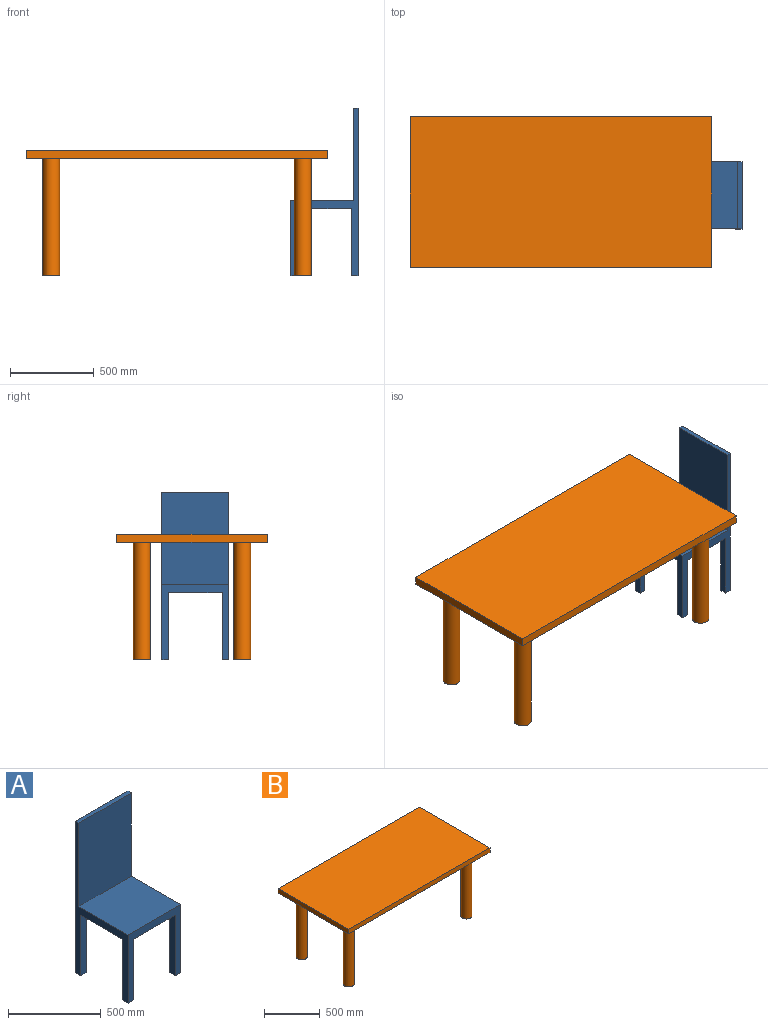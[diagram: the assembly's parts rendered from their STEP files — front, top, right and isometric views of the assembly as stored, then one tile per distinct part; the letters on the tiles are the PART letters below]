
ASSEMBLY  parts=2 mates=1
PART A: 20 faces, bbox 400x400x1000 mm
  f0: plane 1000x400mm, normal (1,0,0), area 65750mm2, adj f1,f3,f4,f5,f6,f7,f15,f16
  f1: plane 1000x400mm, normal (0,1,0), area 272000mm2, adj f0,f2,f4,f7,f11,f13,f18,f19
  f2: plane 1000x400mm, normal (-1,0,0), area 65750mm2, adj f1,f3,f4,f5,f6,f7,f8,f10
  f3: plane 450x400mm, normal (0,-1,0), area 52000mm2, adj f0,f2,f4,f5,f9,f10,f14,f16
  f4: plane 400x400mm, normal (0,0,-1), area 153600mm2, adj f0,f1,f2,f3,f8,f9,f11,f12
  f5: plane 400x375mm, normal (0,0,1), area 150000mm2, adj f0,f2,f3,f6
  f6: plane 550x400mm, normal (0,-1,0), area 220000mm2, adj f0,f2,f5,f7
  f7: plane 400x25mm, normal (0,0,1), area 10000mm2, adj f0,f1,f2,f6
  f8: plane 400x40mm, normal (0,1,0), area 16000mm2, adj f2,f4,f9,f10
  f9: plane 400x40mm, normal (1,0,0), area 16000mm2, adj f3,f4,f8,f10
  f10: plane 40x40mm, normal (0,0,-1), area 1600mm2, adj f2,f3,f8,f9
  f11: plane 400x40mm, normal (1,0,0), area 16000mm2, adj f1,f4,f12,f13
  f12: plane 400x40mm, normal (0,-1,0), area 16000mm2, adj f2,f4,f11,f13
  f13: plane 40x40mm, normal (0,0,-1), area 1600mm2, adj f1,f2,f11,f12
  f14: plane 400x40mm, normal (-1,0,0), area 16000mm2, adj f3,f4,f15,f16
  f15: plane 400x40mm, normal (0,1,0), area 16000mm2, adj f0,f4,f14,f16
  f16: plane 40x40mm, normal (0,0,-1), area 1600mm2, adj f0,f3,f14,f15
  f17: plane 400x40mm, normal (0,-1,0), area 16000mm2, adj f0,f4,f18,f19
  f18: plane 400x40mm, normal (-1,0,0), area 16000mm2, adj f1,f4,f17,f19
  f19: plane 40x40mm, normal (0,0,-1), area 1600mm2, adj f0,f1,f17,f18
PART B: 14 faces, bbox 1800x900x750 mm
  f0: plane 900x50mm, normal (1,0,0), area 45000mm2, adj f1,f3,f4,f5
  f1: plane 1800x50mm, normal (0,1,0), area 90000mm2, adj f0,f2,f4,f5
  f2: plane 900x50mm, normal (-1,0,0), area 45000mm2, adj f1,f3,f4,f5
  f3: plane 1800x50mm, normal (0,-1,0), area 90000mm2, adj f0,f2,f4,f5
  f4: plane 1800x900mm, normal (0,0,1), area 1620000mm2, adj f0,f1,f2,f3
  f5: plane 1800x900mm, normal (0,0,-1), area 1588584.1mm2, adj f0,f1,f2,f3,f6,f8,f10,f12
  f6: cylinder r=50mm len=700mm, axis (0,0,1), area 219911.5mm2, adj f5,f7
  f7: plane 100x100mm, normal (0,0,-1), area 7854mm2, adj f6
  f8: cylinder r=50mm len=700mm, axis (0,0,1), area 219911.5mm2, adj f5,f9
  f9: plane 100x100mm, normal (0,0,-1), area 7854mm2, adj f8
  f10: cylinder r=50mm len=700mm, axis (0,0,1), area 219911.5mm2, adj f5,f11
  f11: plane 100x100mm, normal (0,0,-1), area 7854mm2, adj f10
  f12: cylinder r=50mm len=700mm, axis (0,0,1), area 219911.5mm2, adj f5,f13
  f13: plane 100x100mm, normal (0,0,-1), area 7854mm2, adj f12
PLACE A rot(axis=(0,0,-1),90deg) t=(880,-20,-250)mm
PLACE B at identity fixed
MATE planar A.f16 <-> B.f10  axis (0,0,-1) through (700,-200,-700)mm
